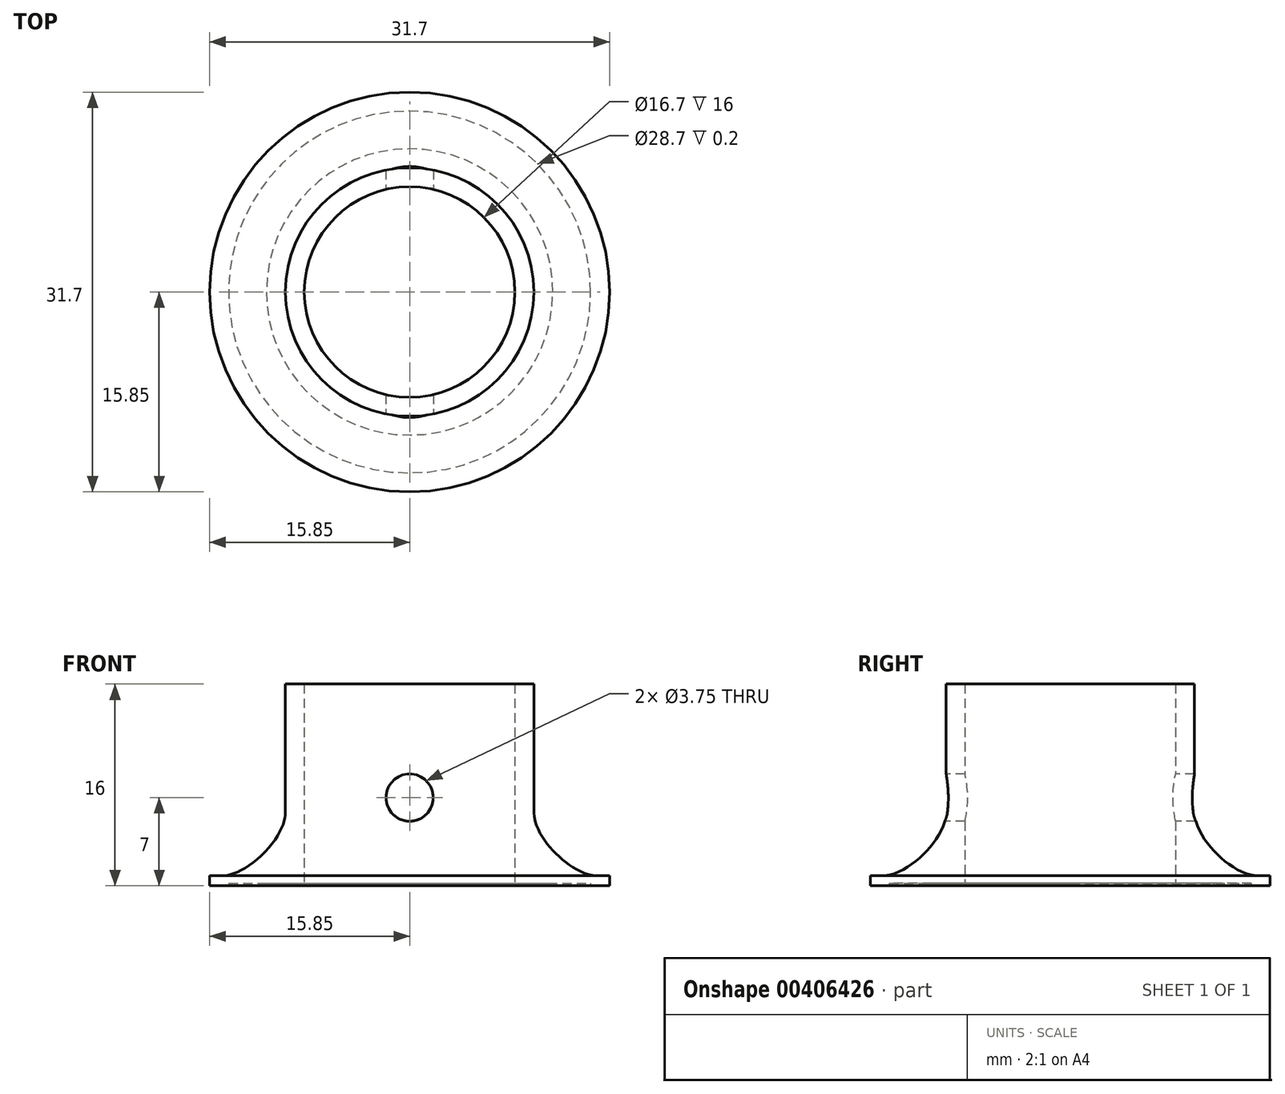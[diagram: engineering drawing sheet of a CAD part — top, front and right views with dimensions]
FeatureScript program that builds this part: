
annotation { "Feature Type Name" : "Feature", "Feature Type Description" : "" }
export const myFeature = defineFeature(function(context is Context, id is Id, definition is map)
    precondition{}
    {
        {
            var Q0;
            Q0=qCreatedBy(makeId("Front.planeOp"),FACE);
            var sketch = newSketch(context, id + "F0", { "sketchPlane" : qUnion([Q0])});
            skLineSegment(sketch, "E0", {"start": v(-15.85, 0) * mm, "end": v(-8.35, 0) * mm});
            skLineSegment(sketch, "E1", {"start": v(-8.35, 0) * mm, "end": v(-8.35, 16) * mm});
            skLineSegment(sketch, "E2", {"start": v(-8.35, 16) * mm, "end": v(-9.85, 16) * mm});
            skLineSegment(sketch, "E3", {"start": v(-9.85, 16) * mm, "end": v(-9.85, 0.8) * mm});
            skLineSegment(sketch, "E4", {"start": v(-9.85, 0.8) * mm, "end": v(-15.85, 0.8) * mm});
            skLineSegment(sketch, "E5", {"start": v(-15.85, 0.8) * mm, "end": v(-15.85, 0) * mm});
            skLineSegment(sketch, "E6.bottom", {"start": v(-14.35, 0.2) * mm, "end": v(-11.35, 0.2) * mm});
            skLineSegment(sketch, "E6.top", {"start": v(-14.35, 0) * mm, "end": v(-11.35, 0) * mm});
            skLineSegment(sketch, "E6.left", {"start": v(-14.35, 0.2) * mm, "end": v(-14.35, 0) * mm});
            skLineSegment(sketch, "E6.right", {"start": v(-11.35, 0.2) * mm, "end": v(-11.35, 0) * mm});
            skLineSegment(sketch, "E7", {"start": v(0, 0) * mm, "end": v(0, 16) * mm, "construction": true});
            skCircle(sketch, "E8", {"center": v(0, 7) * mm, "radius": 1.88 * mm});
            skSolve(sketch);
        }
        {
            var Q0;
            {var subQ0=sQuery(id+"F0.wireOp",EDGE,"E1");Q0=makeQuery(id+"F0.imprint","IMPRINT",FACE,{"disambiguationData":[TD([[makeQuery(id+"F0.imprint","IMPRINT",EDGE,{"derivedFrom":subQ0}),1.0]])]});}
            var Q1;
            Q1=sQuery(id+"F0.wireOp",EDGE,"E7");
            revolve(context, id + "F1", {"entities" : qUnion([Q0]), "axis" : qUnion([Q1]), "revolveType" : RevolveType.FULL});
        }
        {
            var Q0;
            Q0=makeQuery(id+"F1.opRevolve","SWEPT_EDGE",EDGE,{"disambiguationData":[OSD([sQuery(id+"F0.wireOp",EDGE,"E3"),sQuery(id+"F0.wireOp",EDGE,"E4")])]});
            fillet(context, id + "F2", {"entities" : qUnion([Q0]), "radius" : 5 * mm, "tangentPropagation" : true, "rho" : 0.3, "crossSection" : FilletCrossSection.CONIC, "allowEdgeOverflow" : false});
        }
        {
            var Q0;
            Q0=makeQuery(id+"F0.imprint","IMPRINT",FACE,{"disambiguationData":[TD([[makeQuery(id+"F0.imprint","IMPRINT",EDGE,{"derivedFrom":sQuery(id+"F0.wireOp",EDGE,"E8")}),1.0]])]});
            extrude(context, id + "F3", {"entities" : qUnion([Q0]), "operationType" : NewBodyOperationType.REMOVE, "endBound" : BoundingType.THROUGH_ALL, "oppositeDirection" : true, "depth" : 25 * mm, "hasSecondDirection" : true, "secondDirectionBound" : SecondDirectionBoundingType.THROUGH_ALL, "secondDirectionOppositeDirection" : false, "secondDirectionDepth" : 25 * mm});
        }
    });
